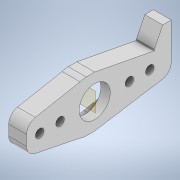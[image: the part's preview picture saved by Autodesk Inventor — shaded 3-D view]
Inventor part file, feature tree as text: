
AUTODESK INVENTOR PART (.ipt)
format: ipt  version: 2020 (Build 240168000, 168)  size: 243,200 bytes
history: native  units: in
note: dims shown in document units (in); Inventor stores cm internally (conversion verified against a paired STEP export)
features: extrude x7, sketch x7, fillet x3, mirror x2, plane x1, chamfer x1
ambient origin geometry x8: Origin, YZ Plane, XZ Plane, XY Plane, X Axis, Y Axis, Z Axis, Center Point
bodies: Solid1 (feature_tree)
feature tree (21):
  extrude  "Extrusion1"  Depth=0.3in
  extrude  "Extrusion2"  Depth=0.3in
  fillet  "Fillet1"  Radius=0.9in
  sketch  "Sketch3"  dims[d2=0.3in d3=0.3in d4=0.9in]
  extrude  "Extrusion6"  Depth=0.08in
  extrude  "Extrusion7"  Depth=0.21in
  extrude  "Extrusion8"  Depth=0.2in
  fillet  "Fillet2"  Radius=0.5in
  plane  "Work Plane1"
  mirror  "Mirror1"
  chamfer  "Chamfer3"  Distance=0.1in
  extrude  "Extrusion9"  Depth=0.3in
  extrude  "Extrusion10"  Depth=0.1in
  mirror  "Mirror2"
  fillet  "Fillet3"  Radius=0.21in
  sketch  "Sketch2"  dims[d0=0.242in d1=0.3in]
  sketch  "Sketch7"  dims[d5=0.2in d6=0.08in]
  sketch  "Sketch8"  dims[d7=0.21in d8=0.0in d9=0.366in]
  sketch  "Sketch9"  dims[d10=0.21in d11=0.0in d12=0.2in d33=0.5in]
  sketch  "Sketch10"  dims[d34=0.6475in]
  sketch  "Sketch11"  dims[d35=0.25in d36=0.1in d37=0.0in d38=0.3in d39=0.1in d40=0.21in d41=0.0in d42=0.21in d43=0.0in d44=0.125in d45=-0.3in d46=0.6475in d47=0.1in d48=0.2in d49=45.0deg d50=0.1in d51=0.24in d52=0.21in d53=0.0in d54=0.0in d55=0.123in d56=0.0in d57=0.8in d58=0.21in d59=0.0in d60=0.125in]
